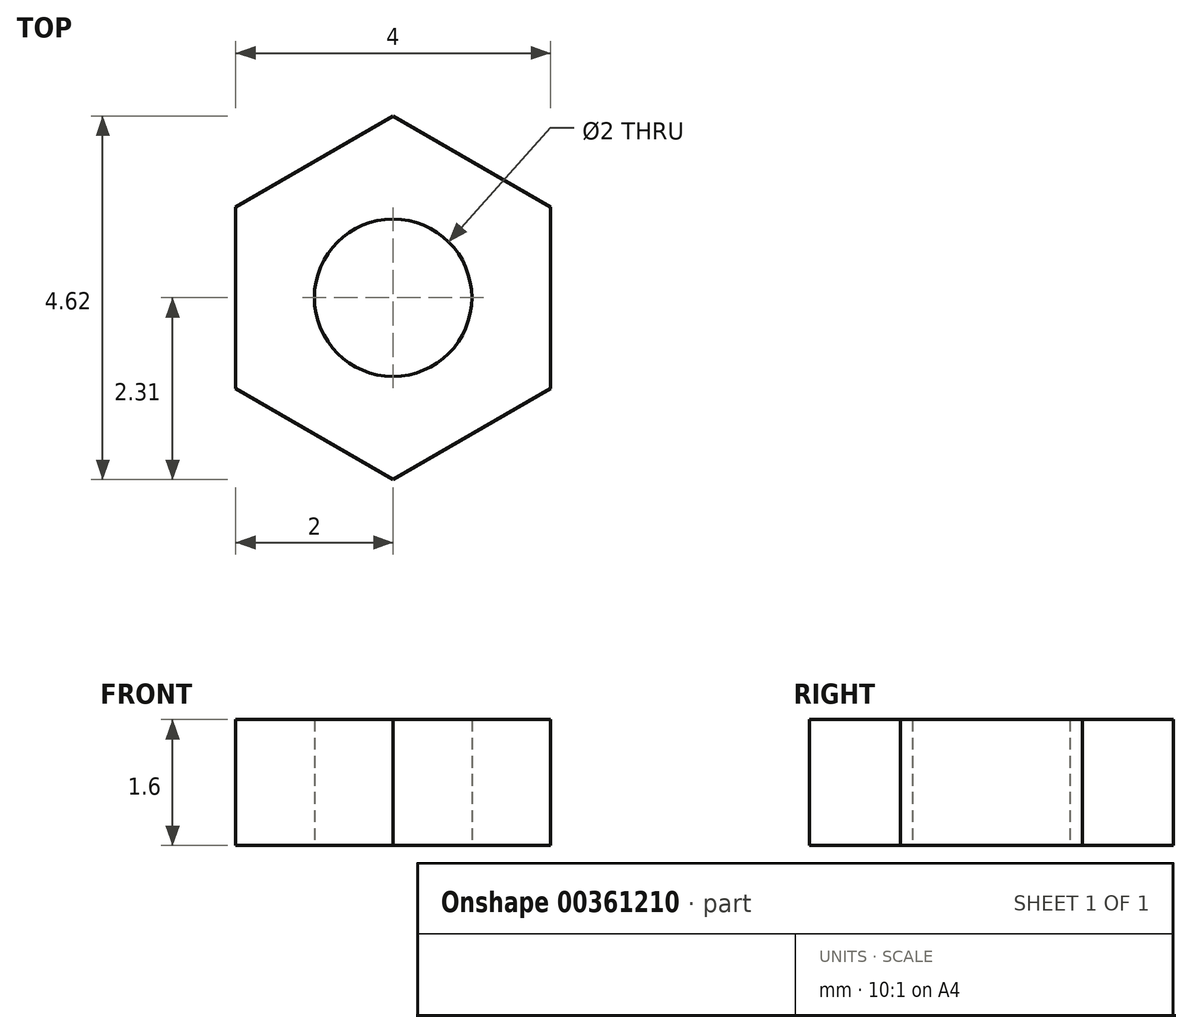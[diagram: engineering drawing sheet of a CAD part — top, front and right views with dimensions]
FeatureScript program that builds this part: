
annotation { "Feature Type Name" : "Feature", "Feature Type Description" : "" }
export const myFeature = defineFeature(function(context is Context, id is Id, definition is map)
    precondition{}
    {
        {
            var Q0;
            Q0=qCreatedBy(makeId("Top.planeOp"),FACE);
            var sketch = newSketch(context, id + "F0", { "sketchPlane" : qUnion([Q0])});
            skCircle(sketch, "E0.cCircle", {"center": v(0, 0) * mm, "radius": 2 * mm, "construction": true});
            skLineSegment(sketch, "E0.0", {"start": v(2, 1.15) * mm, "end": v(2, -1.15) * mm});
            skLineSegment(sketch, "E0.1", {"start": v(2, -1.15) * mm, "end": v(0, -2.3) * mm});
            skLineSegment(sketch, "E0.2", {"start": v(0, -2.3) * mm, "end": v(-2, -1.15) * mm});
            skLineSegment(sketch, "E0.3", {"start": v(-2, -1.15) * mm, "end": v(-2, 1.15) * mm});
            skLineSegment(sketch, "E0.4", {"start": v(-2, 1.15) * mm, "end": v(0, 2.3) * mm});
            skLineSegment(sketch, "E0.5", {"start": v(0, 2.3) * mm, "end": v(2, 1.15) * mm});
            skPoint(sketch, "E0.0.midPoint", {"position": v(2, 0) * mm});
            skCircle(sketch, "E1", {"center": v(0, 0) * mm, "radius": 1 * mm});
            skSolve(sketch);
        }
        {
            var Q0;
            Q0 = qSketchRegion(id + "F0", true);
            extrude(context, id + "F1", {"entities" : qUnion([Q0]), "depth" : 1.6 * mm, "offsetDistance" : 25 * mm});
        }
    });
